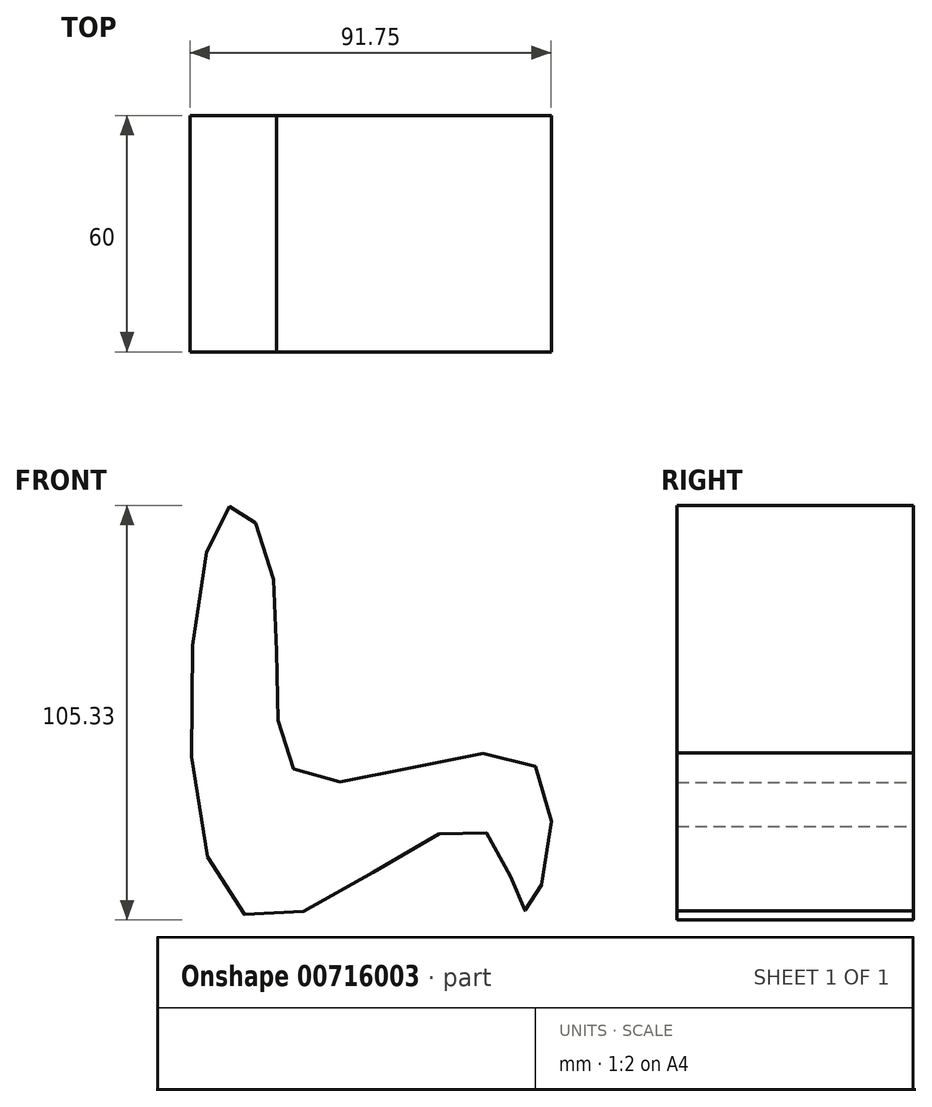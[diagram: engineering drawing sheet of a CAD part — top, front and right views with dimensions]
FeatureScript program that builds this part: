
annotation { "Feature Type Name" : "Feature", "Feature Type Description" : "" }
export const myFeature = defineFeature(function(context is Context, id is Id, definition is map)
    precondition{}
    {
        {
            var Q0;
            Q0=qCreatedBy(makeId("Front.planeOp"),FACE);
            var sketch = newSketch(context, id + "F0", { "sketchPlane" : qUnion([Q0])});
            skFitSpline(sketch, "E0", {"points": [v(-36.38, 34.66) * mm, v(-27.6, -15.94) * mm, v(30.27, -12.89) * mm, v(27.97, -49.55) * mm, v(15.75, -28.55) * mm, v(-43.63, -50.5) * mm, v(-48.79, 52.23) * mm, v(-36.38, 34.66) * mm]});
            skSolve(sketch);
        }
        {
            var Q0;
            Q0=makeQuery(id+"F0.imprint","IMPRINT",FACE,{"disambiguationData":[TD([[makeQuery(id+"F0.imprint","IMPRINT",EDGE,{"derivedFrom":sQuery(id+"F0.wireOp",EDGE,"E0")}),-1.0]])]});
            extrude(context, id + "F1", {"entities" : qUnion([Q0]), "depth" : 60 * mm, "offsetDistance" : 25.4 * mm});
        }
        {
            var Q0;
            Q0=qCreatedBy(makeId("Front.planeOp"),FACE);
            var sketch = newSketch(context, id + "F2", { "sketchPlane" : qUnion([Q0])});
            skFitSpline(sketch, "E1", {"points": [v(-34.67, 9.37) * mm, v(-12.93, 11.16) * mm, v(-6.38, 6.52) * mm, v(-33.85, 0) * mm, v(-34.23, 0) * mm], "startDerivative": vector(64.28, 13.83) * mm, "endDerivative": vector(-2.57, 0.79) * mm});
            skSolve(sketch);
        }
        {
            var Q0;
            Q0=sQuery(id+"F2.wireOp",EDGE,"E1");
            extrude(context, id + "F3", {"bodyType" : ToolBodyType.SURFACE, "surfaceEntities" : qUnion([Q0]), "depth" : 15 * mm, "offsetDistance" : 25.4 * mm});
        }
        {
            var Q0;
            Q0=qCreatedBy(makeId("Front.planeOp"),FACE);
            cPlane(context, id + "F4", {"entities" : qUnion([Q0]), "cplaneType" : CPlaneType.OFFSET, "offset" : 30 * mm, "width" : 152.4 * mm, "height" : 152.4 * mm});
        }
        {
            var Q0;
            Q0=makeQuery(id+"F3.opExtrude","SWEPT_BODY",BODY,{"disambiguationData":[OSD([sQuery(id+"F2.wireOp",EDGE,"E1")])]});
            var Q1;
            Q1=qCreatedBy(id+"F4.planeOp",FACE);
            mirror(context, id + "F5", {"entities" : qUnion([Q0]), "mirrorPlane" : qUnion([Q1])});
        }
    });
